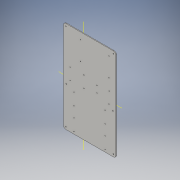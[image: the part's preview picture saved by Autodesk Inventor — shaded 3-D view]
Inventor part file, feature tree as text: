
AUTODESK INVENTOR PART (.ipt)
format: ipt  version: 2016 (Build 200138000, 138)  size: 192,512 bytes
history: native  units: in
note: dims shown in document units (in); Inventor stores cm internally (conversion verified against a paired STEP export)
features: extrude x1, sketch x1
ambient origin geometry x8: Origin, YZ Plane, XZ Plane, XY Plane, X Axis, Y Axis, Z Axis, Center Point
bodies: Body1 (feature_tree)
feature tree (2):
  extrude  "Extrusion3"  Depth=0.125in
  sketch  "Sketch1"  dims[d0=0.0209in d48=7.75in d49=3.8in d61=3.3465in d62=2.2047in d67=1.1in d69=2.0in d71=0.2in d72=0.05in d85=0.6in d87=0.05in d88=0.1in d89=2.7in d90=2.1in d91=0.1in d92=0.1in d93=5.4331in d94=2.2047in d97=0.7874in d99=0.7874in d101=0.7874in d103=0.7874in d105=0.7874in d107=0.7874in d119=2.0in d122=0.4in d126=0.7874in d128=0.7874in d130=0.7874in d132=0.7874in d134=0.7874in d136=0.7874in d144=0.0209in d148=0.7874in d150=0.7874in d152=0.7874in d154=0.7874in d156=0.7874in d158=0.7874in d170=1.25in d171=1.5in d175=0.7874in d177=0.7874in d179=0.7874in d181=0.7874in d183=0.7874in d185=0.7874in d208=0.1in d209=2.205in d210=5.433in d212=0.12in d213=0.7874in d215=3.15in d216=0.7874in d218=4.724in d221=0.12in d222=0.7874in d224=2.283in d225=0.7874in d227=1.929in d230=0.12in d231=0.12in d232=0.12in d233=0.12in d234=0.12in d235=0.7874in d237=1.965in d238=0.7874in d240=5.197in d243=0.12in d244=0.7874in d246=1.965in d247=0.7874in d249=5.197in d256=0.75in d259=0.5in d261=0.16in d262=0.7874in d264=7.95in d265=0.7874in d267=14.51in d271=0.16in d272=0.16in d273=0.5in d274=0.5in d277=0.125in d278=0.0in d280=0.34in d283=0.1378in d284=0.1378in d285=0.2in d287=1.65in d288=1.65in d289=0.25in d290=1.5in]
